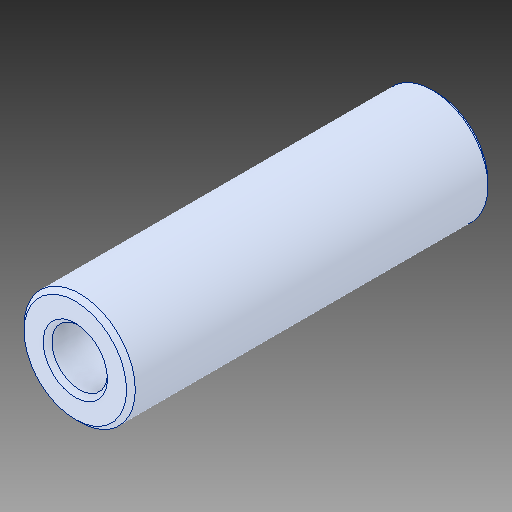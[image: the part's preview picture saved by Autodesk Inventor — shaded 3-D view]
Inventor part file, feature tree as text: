
AUTODESK INVENTOR PART (.ipt)
format: ipt  version: 2017 (Build 210142000, 142)  size: 108,544 bytes
history: native  units: in
note: dims shown in document units (in); Inventor stores cm internally (conversion verified against a paired STEP export)
features: chamfer x1
ambient origin geometry x8: Origin, YZ Plane, XZ Plane, XY Plane, X Axis, Y Axis, Z Axis, Center Point
bodies: Solid1 (feature_tree)
feature tree (1):
  chamfer  "Chamfer1"  [1 undecoded]
note: 1 required parameter value undecoded (feature->parameter linkage not recoverable at this tier; creation-order binding heuristic only, values carry confidence <= 0.55)
